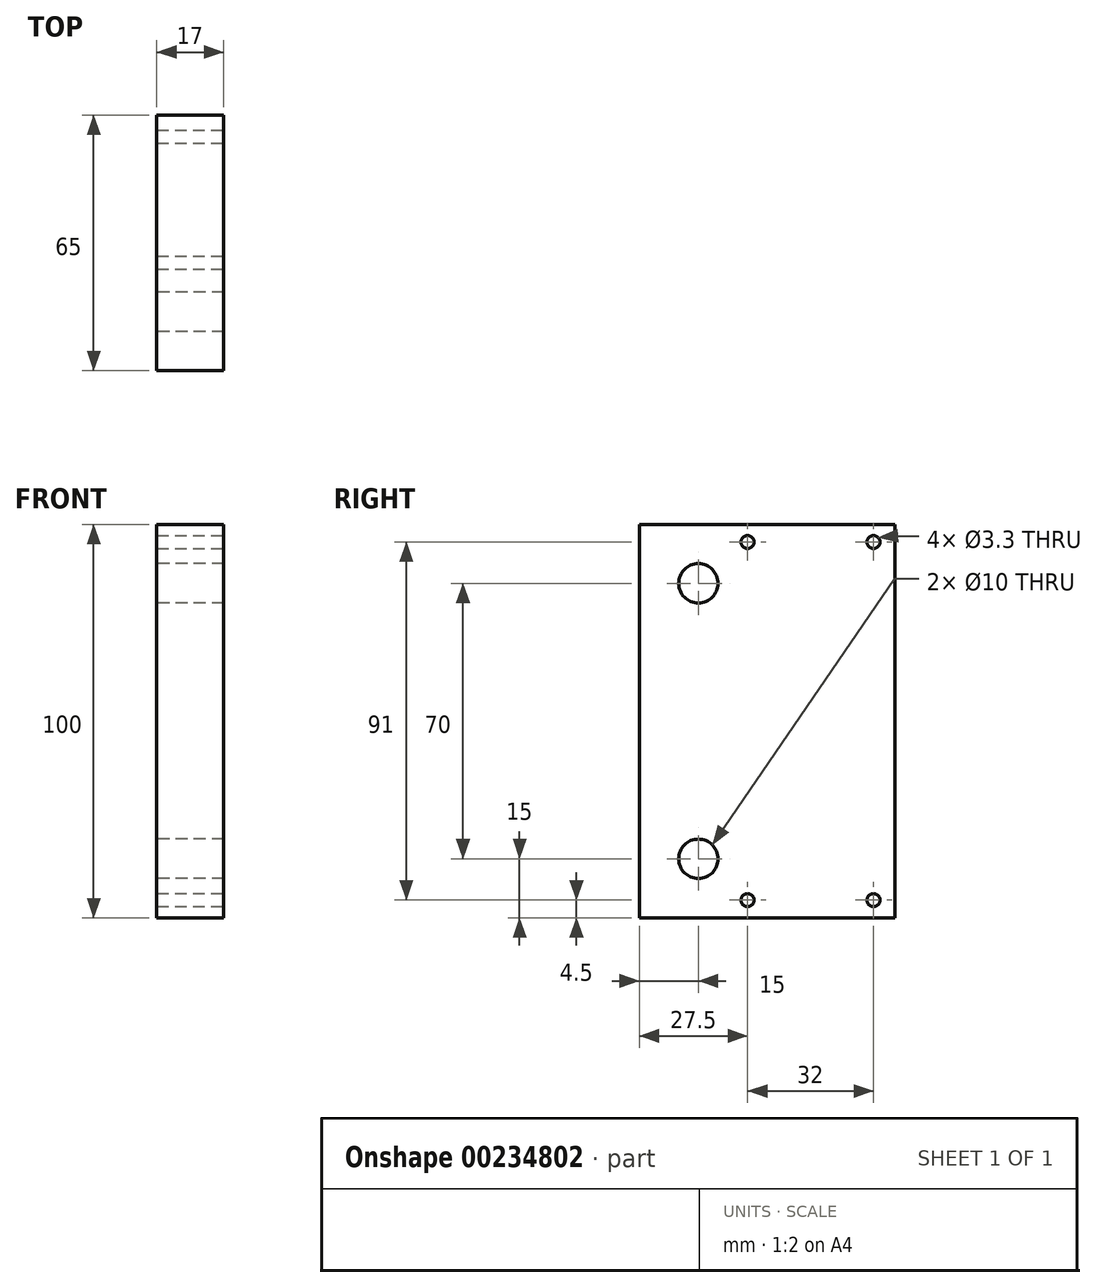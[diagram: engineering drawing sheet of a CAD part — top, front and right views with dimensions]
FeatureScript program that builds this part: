
annotation { "Feature Type Name" : "Feature", "Feature Type Description" : "" }
export const myFeature = defineFeature(function(context is Context, id is Id, definition is map)
    precondition{}
    {
        {
            var Q0;
            Q0=qCreatedBy(makeId("Right.planeOp"),FACE);
            var sketch = newSketch(context, id + "F0", { "sketchPlane" : qUnion([Q0])});
            skLineSegment(sketch, "E0.bottom", {"start": v(0, 100) * mm, "end": v(43, 100) * mm});
            skLineSegment(sketch, "E0.top", {"start": v(0, 0) * mm, "end": v(43, 0) * mm});
            skLineSegment(sketch, "E0.left", {"start": v(0, 100) * mm, "end": v(0, 0) * mm});
            skLineSegment(sketch, "E0.right", {"start": v(43, 100) * mm, "end": v(43, 0) * mm});
            skLineSegment(sketch, "E1.bottom", {"start": v(5.5, 95.5) * mm, "end": v(37.5, 95.5) * mm, "construction": true});
            skLineSegment(sketch, "E1.top", {"start": v(5.5, 4.5) * mm, "end": v(37.5, 4.5) * mm, "construction": true});
            skLineSegment(sketch, "E1.left", {"start": v(5.5, 95.5) * mm, "end": v(5.5, 4.5) * mm, "construction": true});
            skLineSegment(sketch, "E1.right", {"start": v(37.5, 95.5) * mm, "end": v(37.5, 4.5) * mm, "construction": true});
            skPoint(sketch, "E2", {"position": v(5.5, 4.5) * mm});
            skPoint(sketch, "E3", {"position": v(37.5, 4.5) * mm});
            skPoint(sketch, "E4", {"position": v(37.5, 95.5) * mm});
            skPoint(sketch, "E5", {"position": v(5.5, 95.5) * mm});
            skLineSegment(sketch, "E6", {"start": v(43, 67) * mm, "end": v(80.5, 67) * mm});
            skLineSegment(sketch, "E7", {"start": v(80.5, 67) * mm, "end": v(80.5, 33) * mm});
            skLineSegment(sketch, "E8", {"start": v(80.5, 33) * mm, "end": v(43, 33) * mm});
            skLineSegment(sketch, "E9.bottom", {"start": v(49.5, 60) * mm, "end": v(73.5, 60) * mm, "construction": true});
            skLineSegment(sketch, "E9.top", {"start": v(49.5, 40) * mm, "end": v(73.5, 40) * mm, "construction": true});
            skLineSegment(sketch, "E9.left", {"start": v(49.5, 60) * mm, "end": v(49.5, 40) * mm, "construction": true});
            skLineSegment(sketch, "E9.right", {"start": v(73.5, 60) * mm, "end": v(73.5, 40) * mm, "construction": true});
            skPoint(sketch, "E10", {"position": v(49.5, 60) * mm});
            skPoint(sketch, "E11", {"position": v(73.5, 60) * mm});
            skPoint(sketch, "E12", {"position": v(73.5, 40) * mm});
            skPoint(sketch, "E13", {"position": v(49.5, 40) * mm});
            skSolve(sketch);
        }
        {
            var Q0;
            {var subQ1=sQuery(id+"F0.wireOp",EDGE,"E0.bottom");Q0=makeQuery(id+"F0.imprint","IMPRINT",FACE,{"disambiguationData":[TD([[makeQuery(id+"F0.imprint","IMPRINT",EDGE,{"derivedFrom":subQ1}),-1.0]])]});}
            extrude(context, id + "F1", {"entities" : qUnion([Q0]), "oppositeDirection" : true, "depth" : 17 * mm});
        }
        {
            var Q0;
            Q0=sQuery(id+"F0.wireOp",VERTEX,"E3");
            var Q1;
            Q1=sQuery(id+"F0.wireOp",VERTEX,"E2");
            var Q2;
            Q2=sQuery(id+"F0.wireOp",VERTEX,"E5");
            var Q3;
            Q3=sQuery(id+"F0.wireOp",VERTEX,"E4");
            var Q4;
            Q4=makeQuery(id+"F1.opExtrude","SWEPT_BODY",BODY,{"disambiguationData":[OSD([sQuery(id+"F0.wireOp",EDGE,"E0.bottom"),sQuery(id+"F0.wireOp",EDGE,"E0.top"),sQuery(id+"F0.wireOp",EDGE,"E0.left"),sQuery(id+"F0.wireOp",EDGE,"E0.right")])]});
            hole(context, id + "F2", {"style" : HoleStyle.SIMPLE, "endStyle" : HoleEndStyle.THROUGH, "standardTappedOrClearance" : lookupTablePath({ "standard" : "ISO", "fit" : "Normal", "size" : "M3", "type" : "Clearance" }), "standardBlindInLast" : lookupTablePath({ "fit" : "Standard", "standard" : "ISO", "size" : "M3", "type" : "Clearance" }), "holeDiameter" : 3.3 * mm, "startFromSketch" : true, "locations" : qUnion([Q0, Q1, Q2, Q3]), "scope" : qUnion([Q4]), "isTappedThrough" : true});
        }
        {
            var Q0;
            Q0=makeQuery(id+"F1.opExtrude","CAP_FACE",FACE,{"disambiguationData":[OSD([sQuery(id+"F0.wireOp",EDGE,"E0.bottom"),sQuery(id+"F0.wireOp",EDGE,"E0.top"),sQuery(id+"F0.wireOp",EDGE,"E0.left"),sQuery(id+"F0.wireOp",EDGE,"E0.right")])],"isStart":false});
            var sketch = newSketch(context, id + "F3", { "sketchPlane" : qUnion([Q0])});
            skLineSegment(sketch, "E14.bottom", {"start": v(0, 100) * mm, "end": v(22, 100) * mm});
            skLineSegment(sketch, "E14.top", {"start": v(0, 0) * mm, "end": v(22, 0) * mm});
            skLineSegment(sketch, "E14.left", {"start": v(0, 100) * mm, "end": v(0, 0) * mm});
            skLineSegment(sketch, "E14.right", {"start": v(22, 100) * mm, "end": v(22, 0) * mm});
            skCircle(sketch, "E15", {"center": v(7, 85) * mm, "radius": 5 * mm});
            skCircle(sketch, "E16", {"center": v(7, 15) * mm, "radius": 5 * mm});
            skSolve(sketch);
        }
        {
            var Q0;
            Q0=makeQuery(id+"F3.imprint","IMPRINT",FACE,{"disambiguationData":[TD([[makeQuery(id+"F3.imprint","IMPRINT",EDGE,{"derivedFrom":sQuery(id+"F3.wireOp",EDGE,"E14.bottom")}),-1.0]])]});
            var Q1;
            Q1=makeQuery(id+"F1.opExtrude","CAP_FACE",FACE,{"disambiguationData":[OSD([sQuery(id+"F0.wireOp",EDGE,"E0.bottom"),sQuery(id+"F0.wireOp",EDGE,"E0.top"),sQuery(id+"F0.wireOp",EDGE,"E0.left"),sQuery(id+"F0.wireOp",EDGE,"E0.right")])],"isStart":true});
            extrude(context, id + "F4", {"entities" : qUnion([Q0]), "operationType" : NewBodyOperationType.ADD, "endBound" : BoundingType.UP_TO_SURFACE, "oppositeDirection" : true, "endBoundEntityFace" : qUnion([Q1]), "depth" : 25 * mm});
        }
    });
